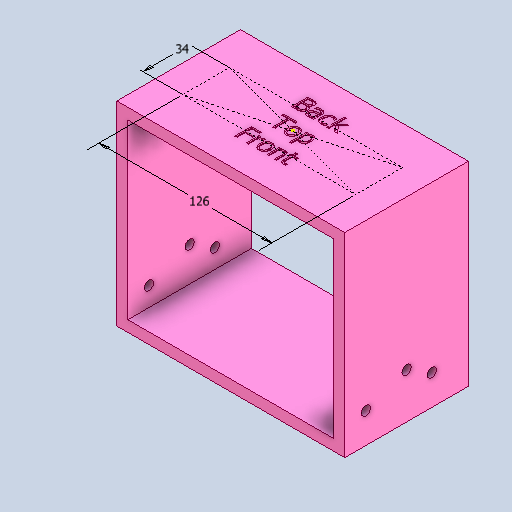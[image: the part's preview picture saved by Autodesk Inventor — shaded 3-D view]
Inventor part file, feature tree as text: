
AUTODESK INVENTOR PART (.ipt)
format: ipt  version: 2022.1 (Build 261234020, 234B)  size: 475,648 bytes
history: native  units: mm
features: sketch x7, extrude x3, hole x2, emboss x1
ambient origin geometry x8: Origin, YZ Plane, XZ Plane, XY Plane, X Axis, Y Axis, Z Axis, Center Point
bodies: Body1 (feature_tree)
feature tree (13):
  extrude  "Extrusion22"  Depth=166.0mm
  extrude  "Extrusion23"  TaperAngle=0.0deg  [1 undecoded]
  emboss  "Emboss1"
  extrude  "Extrusion24"  Depth=8.0mm
  hole  "Hole6"  [1 undecoded]
  hole  "Hole7"  [1 undecoded]
  sketch  "Sketch53"  dims[d230=25.0mm d231=6.756mm d232=6.0mm d233=12.878mm d234=2.0mm d235=14.3117mm d236=8.0mm d237=0.0mm d238=14.0mm d239=18.35mm d240=29.65mm d241=6.756mm d242=6.0mm d243=15.875mm d244=4.826mm d245=14.3117mm d246=9.53mm d247=20.594885mm d248=34.0mm d249=126.0mm d64=1.0mm d65=1.0mm d66=1.0mm d67=0.15mm d68=0.25mm d69=0.375mm d70=14.3117mm d71=0.75mm d72=20.594885mm d73=0.0625mm d74=0.75mm d75=0.375mm]
  sketch  "Sketch47"  dims[d218=90.0mm d219=166.0mm]
  sketch  "Sketch48"  dims[d220=8.0mm d221=0.0mm]
  sketch  "Sketch49"  dims[d222=8.0mm d223=8.0mm]
  sketch  "Sketch50"  dims[d224=126.0mm d225=0.0mm]
  sketch  "Sketch51"  dims[d226=1.0mm d227=0.0mm d228=8.0mm]
  sketch  "Sketch52"  dims[d229=0.0mm]
note: 3 required parameter values undecoded (feature->parameter linkage not recoverable at this tier; creation-order binding heuristic only, values carry confidence <= 0.55)
